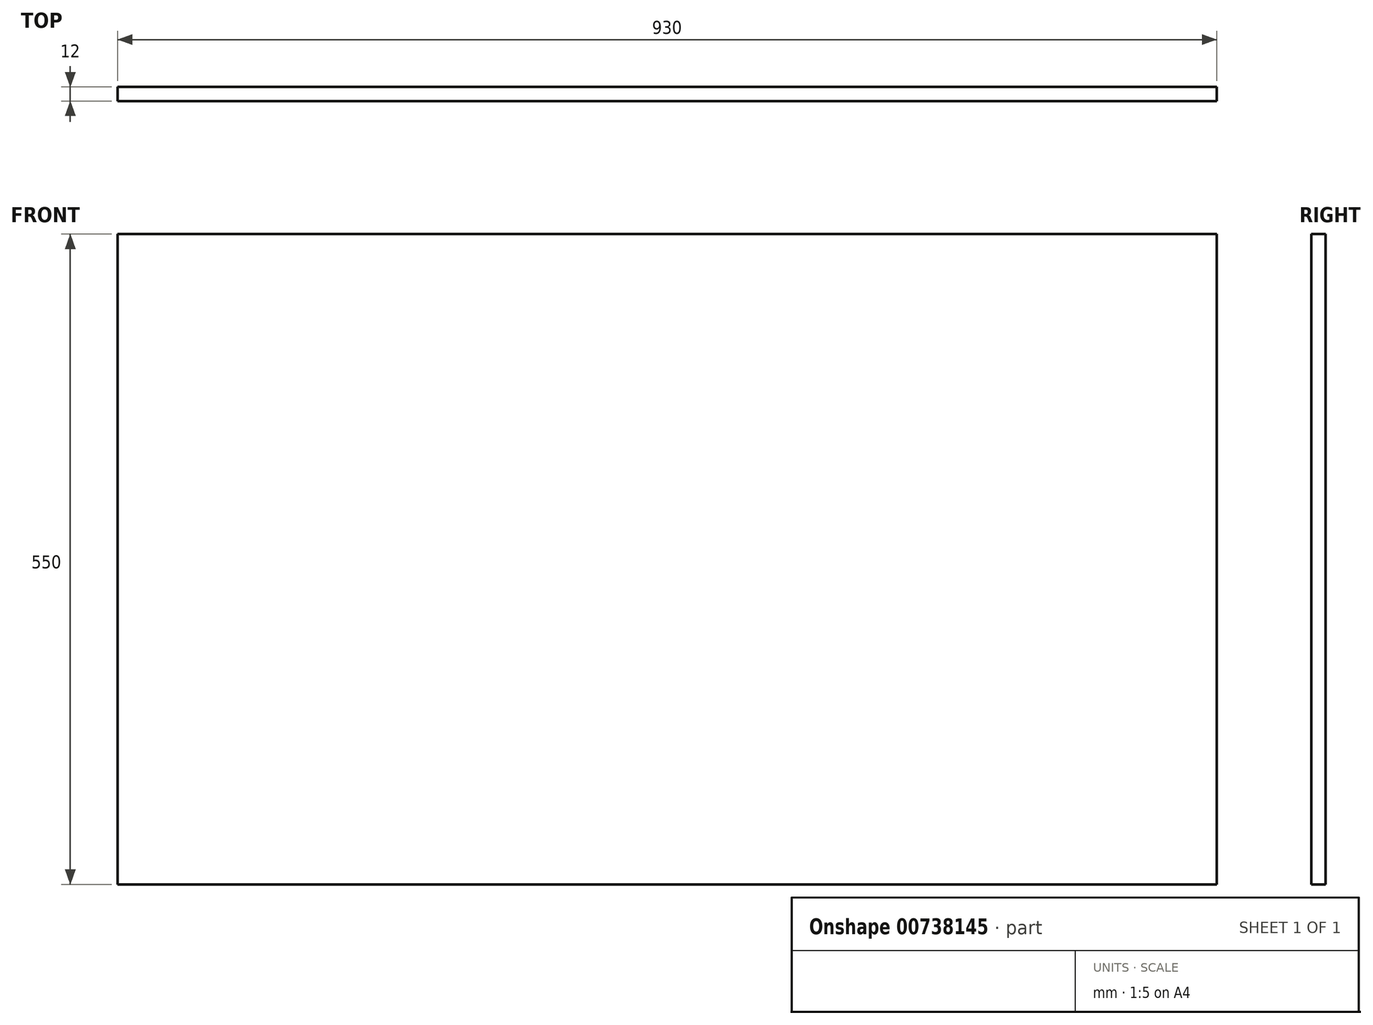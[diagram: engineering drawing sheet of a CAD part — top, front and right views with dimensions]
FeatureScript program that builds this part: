
annotation { "Feature Type Name" : "Feature", "Feature Type Description" : "" }
export const myFeature = defineFeature(function(context is Context, id is Id, definition is map)
    precondition{}
    {
        {
            var Q0;
            Q0=qCreatedBy(makeId("Front.planeOp"),FACE);
            var sketch = newSketch(context, id + "F0", { "sketchPlane" : qUnion([Q0])});
            skLineSegment(sketch, "E0.bottom", {"start": v(-465, -275) * mm, "end": v(465, -275) * mm});
            skLineSegment(sketch, "E0.top", {"start": v(-465, 275) * mm, "end": v(465, 275) * mm});
            skLineSegment(sketch, "E0.left", {"start": v(-465, -275) * mm, "end": v(-465, 275) * mm});
            skLineSegment(sketch, "E0.right", {"start": v(465, -275) * mm, "end": v(465, 275) * mm});
            skPoint(sketch, "E0.middle", {"position": v(0, 0) * mm});
            skSolve(sketch);
        }
        {
            var Q0;
            Q0 = qSketchRegion(id + "F0", true);
            extrude(context, id + "F1", {"entities" : qUnion([Q0]), "depth" : 12 * mm, "offsetDistance" : 25 * mm});
        }
    });
